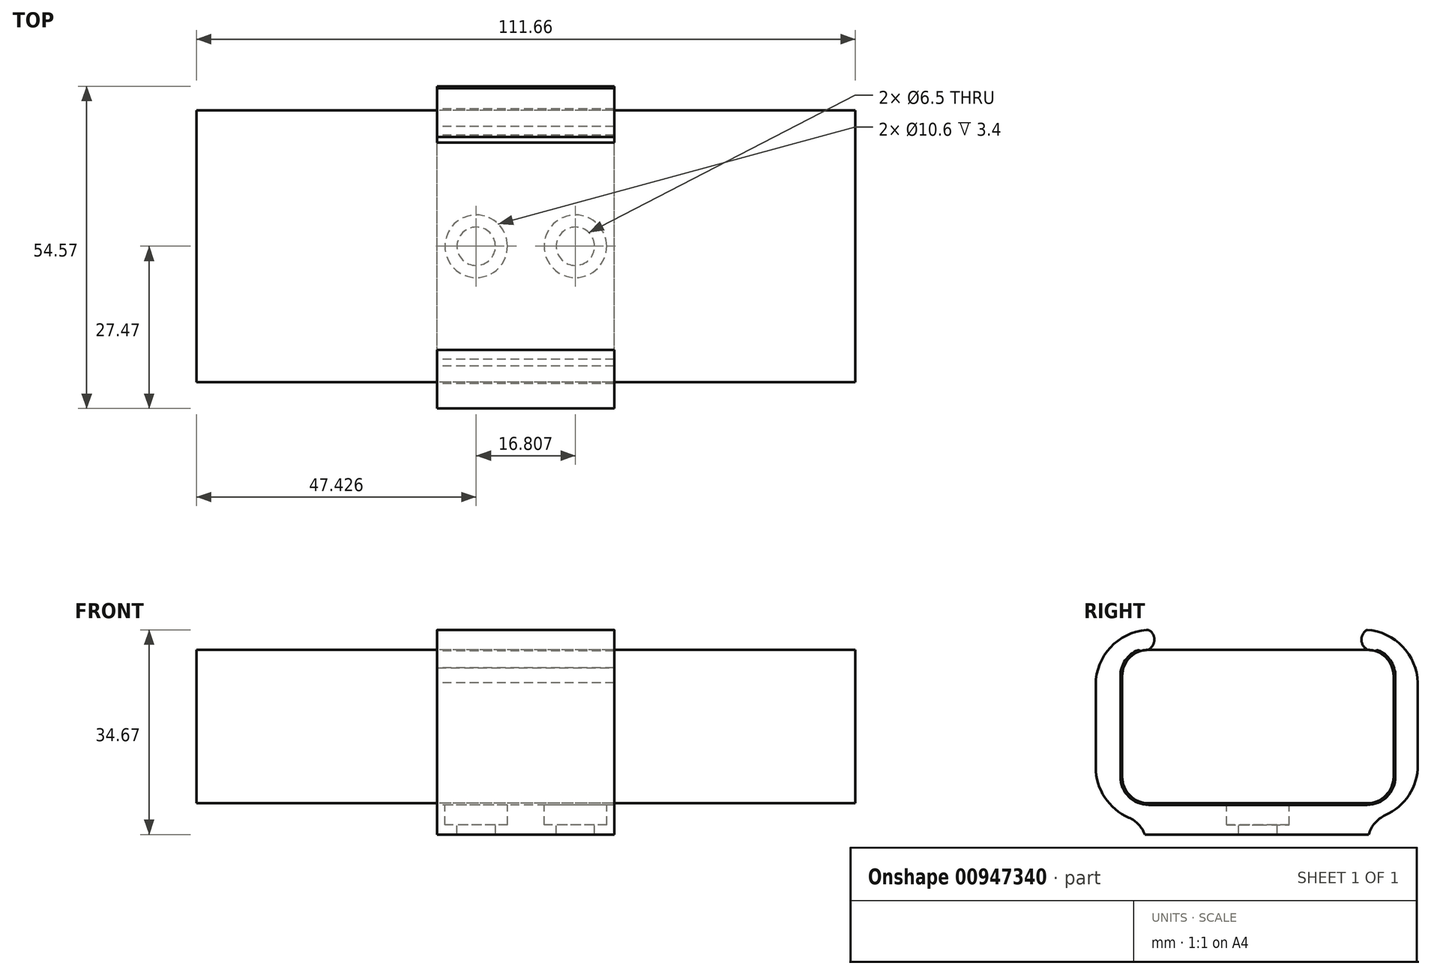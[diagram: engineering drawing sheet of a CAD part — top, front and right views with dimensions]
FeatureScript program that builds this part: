
annotation { "Feature Type Name" : "Feature", "Feature Type Description" : "" }
export const myFeature = defineFeature(function(context is Context, id is Id, definition is map)
    precondition{}
    {
        {
            var Q0;
            Q0=qCreatedBy(makeId("Right.planeOp"),FACE);
            var sketch = newSketch(context, id + "F0", { "sketchPlane" : qUnion([Q0])});
            skLineSegment(sketch, "E0.bottom", {"start": v(-18.5, 0) * mm, "end": v(18.5, 0) * mm});
            skLineSegment(sketch, "E0.top", {"start": v(-18.5, 26) * mm, "end": v(18.5, 26) * mm});
            skLineSegment(sketch, "E0.left", {"start": v(-23, 4.5) * mm, "end": v(-23, 21.5) * mm});
            skLineSegment(sketch, "E0.right", {"start": v(23, 4.5) * mm, "end": v(23, 21.5) * mm});
            skPoint(sketch, "E1.visualSharp", {"position": v(-23, 0) * mm});
            skArc(sketch, "E1.filletArc", {"start": v(-23, 4.5) * mm, "mid": v(-21.68, 1.32) * mm, "end": v(-18.5, 0) * mm});
            skPoint(sketch, "E2.visualSharp", {"position": v(23, 0) * mm});
            skArc(sketch, "E2.filletArc", {"start": v(18.5, 0) * mm, "mid": v(21.68, 1.32) * mm, "end": v(23, 4.5) * mm});
            skPoint(sketch, "E3.visualSharp", {"position": v(-23, 26) * mm});
            skArc(sketch, "E3.filletArc", {"start": v(-18.5, 26) * mm, "mid": v(-21.68, 24.68) * mm, "end": v(-23, 21.5) * mm});
            skPoint(sketch, "E4.visualSharp", {"position": v(23, 26) * mm});
            skArc(sketch, "E4.filletArc", {"start": v(23, 21.5) * mm, "mid": v(21.68, 24.68) * mm, "end": v(18.5, 26) * mm});
            skSolve(sketch);
        }
        {
            var Q0;
            Q0 = qSketchRegion(id + "F0", true);
            extrude(context, id + "F1", {"entities" : qUnion([Q0]), "endBound" : BoundingType.SYMMETRIC, "depth" : 111.65 * mm, "offsetDistance" : 25 * mm});
        }
        {
            var Q0;
            Q0=qCreatedBy(makeId("Right.planeOp"),FACE);
            var sketch = newSketch(context, id + "F2", { "sketchPlane" : qUnion([Q0])});
            skLineSegment(sketch, "E5.0.0", {"start": v(18.5, 26) * mm, "end": v(-18.5, 26) * mm, "construction": true});
            skArc(sketch, "E5.0.1", {"start": v(-18.5, 26) * mm, "mid": v(-21.68, 24.68) * mm, "end": v(-23, 21.5) * mm, "construction": true});
            skLineSegment(sketch, "E5.0.2", {"start": v(-23, 21.5) * mm, "end": v(-23, 4.5) * mm, "construction": true});
            skArc(sketch, "E5.0.3", {"start": v(-23, 4.5) * mm, "mid": v(-21.68, 1.32) * mm, "end": v(-18.5, 0) * mm, "construction": true});
            skLineSegment(sketch, "E5.0.4", {"start": v(-18.5, 0) * mm, "end": v(18.5, 0) * mm, "construction": true});
            skArc(sketch, "E5.0.5", {"start": v(18.5, 0) * mm, "mid": v(21.68, 1.32) * mm, "end": v(23, 4.5) * mm, "construction": true});
            skLineSegment(sketch, "E5.0.6", {"start": v(23, 4.5) * mm, "end": v(23, 21.5) * mm, "construction": true});
            skArc(sketch, "E5.0.7", {"start": v(23, 21.5) * mm, "mid": v(21.68, 24.68) * mm, "end": v(18.5, 26) * mm, "construction": true});
            skLineSegment(sketch, "E6.1", {"start": v(23.3, 4.5) * mm, "end": v(23.3, 21.5) * mm});
            skArc(sketch, "E6.2", {"start": v(18.5, -0.3) * mm, "mid": v(21.9, 1.1) * mm, "end": v(23.3, 4.5) * mm});
            skArc(sketch, "E6.3", {"start": v(-20.3, 25.95) * mm, "mid": v(-22.48, 24.18) * mm, "end": v(-23.3, 21.5) * mm});
            skLineSegment(sketch, "E6.4", {"start": v(-23.3, 21.5) * mm, "end": v(-23.3, 4.5) * mm});
            skArc(sketch, "E6.5", {"start": v(-23.3, 4.5) * mm, "mid": v(-21.9, 1.1) * mm, "end": v(-18.5, -0.3) * mm});
            skLineSegment(sketch, "E6.6", {"start": v(-18.5, -0.3) * mm, "end": v(18.5, -0.3) * mm});
            skLineSegment(sketch, "E7", {"start": v(18.5, 21.5) * mm, "end": v(21.68, 24.68) * mm, "construction": true});
            skArc(sketch, "E8.0", {"start": v(26.74, 22.94) * mm, "mid": v(26.74, 22.95) * mm, "end": v(26.74, 22.95) * mm});
            skLineSegment(sketch, "E8.1", {"start": v(27.1, 6.46) * mm, "end": v(27.1, 20.4) * mm});
            skArc(sketch, "E8.2", {"start": v(18.8, -2.8) * mm, "mid": v(24.72, 0.24) * mm, "end": v(27.1, 6.46) * mm});
            skArc(sketch, "E8.3", {"start": v(-18.49, 29.37) * mm, "mid": v(-24.87, 26.52) * mm, "end": v(-27.47, 20.04) * mm});
            skLineSegment(sketch, "E8.4", {"start": v(-27.47, 20.04) * mm, "end": v(-27.47, 6.09) * mm});
            skArc(sketch, "E8.5", {"start": v(-27.47, 6.09) * mm, "mid": v(-25.1, -0.13) * mm, "end": v(-19.17, -3.16) * mm});
            skFitSpline(sketch, "E9", {"points": [v(21.09, 24.61) * mm, v(26.74, 22.95) * mm, v(26.74, 22.94) * mm], "startDerivative": vector(2.9, 3.8) * mm, "endDerivative": vector(-0.12, 0.4) * mm});
            skLineSegment(sketch, "E10.top", {"start": v(-19.17, -5.3) * mm, "end": v(18.8, -5.3) * mm});
            skLineSegment(sketch, "E10.left", {"start": v(-19.17, -3.16) * mm, "end": v(-19.17, -5.3) * mm});
            skLineSegment(sketch, "E10.right", {"start": v(18.8, -2.8) * mm, "end": v(18.8, -5.3) * mm});
            skArc(sketch, "E11", {"start": v(-20.3, 25.95) * mm, "mid": v(-17.77, 26.8) * mm, "end": v(-18.49, 29.37) * mm});
            skArc(sketch, "E12.0", {"start": v(27.1, 20.4) * mm, "mid": v(24.5, 26.53) * mm, "end": v(18.49, 29.37) * mm});
            skLineSegment(sketch, "E13", {"start": v(0, 26) * mm, "end": v(0, -12.79) * mm, "construction": true});
            skArc(sketch, "E14.MirrorCS", {"start": v(20.3, 25.95) * mm, "mid": v(17.77, 26.8) * mm, "end": v(18.49, 29.37) * mm});
            skPoint(sketch, "E15.orphan", {"position": v(20.3, 25.95) * mm});
            skArc(sketch, "E16", {"start": v(23.3, 21.5) * mm, "mid": v(22.48, 24.18) * mm, "end": v(20.3, 25.95) * mm});
            skSolve(sketch);
        }
        {
            var Q0;
            Q0 = qSketchRegion(id + "F2", true);
            extrude(context, id + "F3", {"entities" : qUnion([Q0]), "endBound" : BoundingType.SYMMETRIC, "depth" : 30 * mm, "offsetDistance" : 25 * mm});
        }
        {
            var Q0;
            Q0=makeQuery(id+"F3.opExtrude","SWEPT_FACE",FACE,{"disambiguationData":[OSD([sQuery(id+"F2.wireOp",EDGE,"E6.6")])]});
            var sketch = newSketch(context, id + "F4", { "sketchPlane" : qUnion([Q0])});
            skPoint(sketch, "E17", {"position": v(8.4, 0) * mm});
            skPoint(sketch, "E18", {"position": v(-8.4, 0) * mm});
            skSolve(sketch);
        }
        {
            var Q0;
            Q0=sQuery(id+"F4.wireOp",VERTEX,"E18");
            var Q1;
            Q1=sQuery(id+"F4.wireOp",VERTEX,"E17");
            var Q2;
            Q2=makeQuery(id+"F3.opExtrude","SWEPT_BODY",BODY,{"disambiguationData":[OSD([sQuery(id+"F2.wireOp",EDGE,"E6.0"),sQuery(id+"F2.wireOp",EDGE,"E6.1"),sQuery(id+"F2.wireOp",EDGE,"E6.2"),sQuery(id+"F2.wireOp",EDGE,"E6.3"),sQuery(id+"F2.wireOp",EDGE,"E6.4"),sQuery(id+"F2.wireOp",EDGE,"E6.5"),sQuery(id+"F2.wireOp",EDGE,"E6.6"),sQuery(id+"F2.wireOp",EDGE,"9Ljhj78s-MYgS-96Co-cpqi-PuXzUSZSZqxz"),sQuery(id+"F2.wireOp",EDGE,"E8.0"),sQuery(id+"F2.wireOp",EDGE,"E8.1"),sQuery(id+"F2.wireOp",EDGE,"E8.2"),sQuery(id+"F2.wireOp",EDGE,"E8.3"),sQuery(id+"F2.wireOp",EDGE,"E8.4"),sQuery(id+"F2.wireOp",EDGE,"E8.5"),sQuery(id+"F2.wireOp",EDGE,"E8.6"),sQuery(id+"F2.wireOp",EDGE,"E9"),sQuery(id+"F2.wireOp",EDGE,"Q8KgLUTt-K49j-rBwW-dHn6-Ze1EflflIzW6"),sQuery(id+"F2.wireOp",EDGE,"MUvmFMtZ-lGsu-43Td-AwhQ-ec3yMmGewe0g.top"),sQuery(id+"F2.wireOp",EDGE,"MUvmFMtZ-lGsu-43Td-AwhQ-ec3yMmGewe0g.left"),sQuery(id+"F2.wireOp",EDGE,"MUvmFMtZ-lGsu-43Td-AwhQ-ec3yMmGewe0g.right"),sQuery(id+"F2.wireOp",EDGE,"9a86af33-fc48-4b77-91b4-7a05d1dd84bc.trimOffspring")])]});
            hole(context, id + "F5", {"style" : HoleStyle.C_BORE, "endStyle" : HoleEndStyle.THROUGH, "holeDiameter" : 6.5 * mm, "cBoreDiameter" : 10.6 * mm, "cBoreDepth" : 3.4 * mm, "majorDiameter" : 5 * mm, "isTappedThrough" : true, "tappedDepth" : 12 * mm, "tapClearance" : 3, "locations" : qUnion([Q0, Q1]), "scope" : qUnion([Q2])});
        }
        {
            var Q0;
            Q0=makeQuery(id+"F3.opExtrude","SWEPT_EDGE",EDGE,{"disambiguationData":[OSD([sQuery(id+"F2.wireOp",EDGE,"E8.2"),sQuery(id+"F2.wireOp",EDGE,"E10.right")])]});
            var Q1;
            Q1=makeQuery(id+"F3.opExtrude","SWEPT_EDGE",EDGE,{"disambiguationData":[OSD([sQuery(id+"F2.wireOp",EDGE,"E8.5"),sQuery(id+"F2.wireOp",EDGE,"E10.left")])]});
            fillet(context, id + "F6", {"entities" : qUnion([Q0, Q1]), "radius" : 5 * mm, "tangentPropagation" : true, "allowEdgeOverflow" : false});
        }
        {
            var Q0;
            Q0=makeQuery(id+"F3.opExtrude","SWEPT_EDGE",EDGE,{"disambiguationData":[OSD([sQuery(id+"F2.wireOp",EDGE,"E8.3"),sQuery(id+"F2.wireOp",EDGE,"Q8KgLUTt-K49j-rBwW-dHn6-Ze1EflflIzW6")])]});
            fillet(context, id + "F7", {"entities" : qUnion([Q0]), "radius" : 1 * mm, "tangentPropagation" : true, "allowEdgeOverflow" : false});
        }
    });
